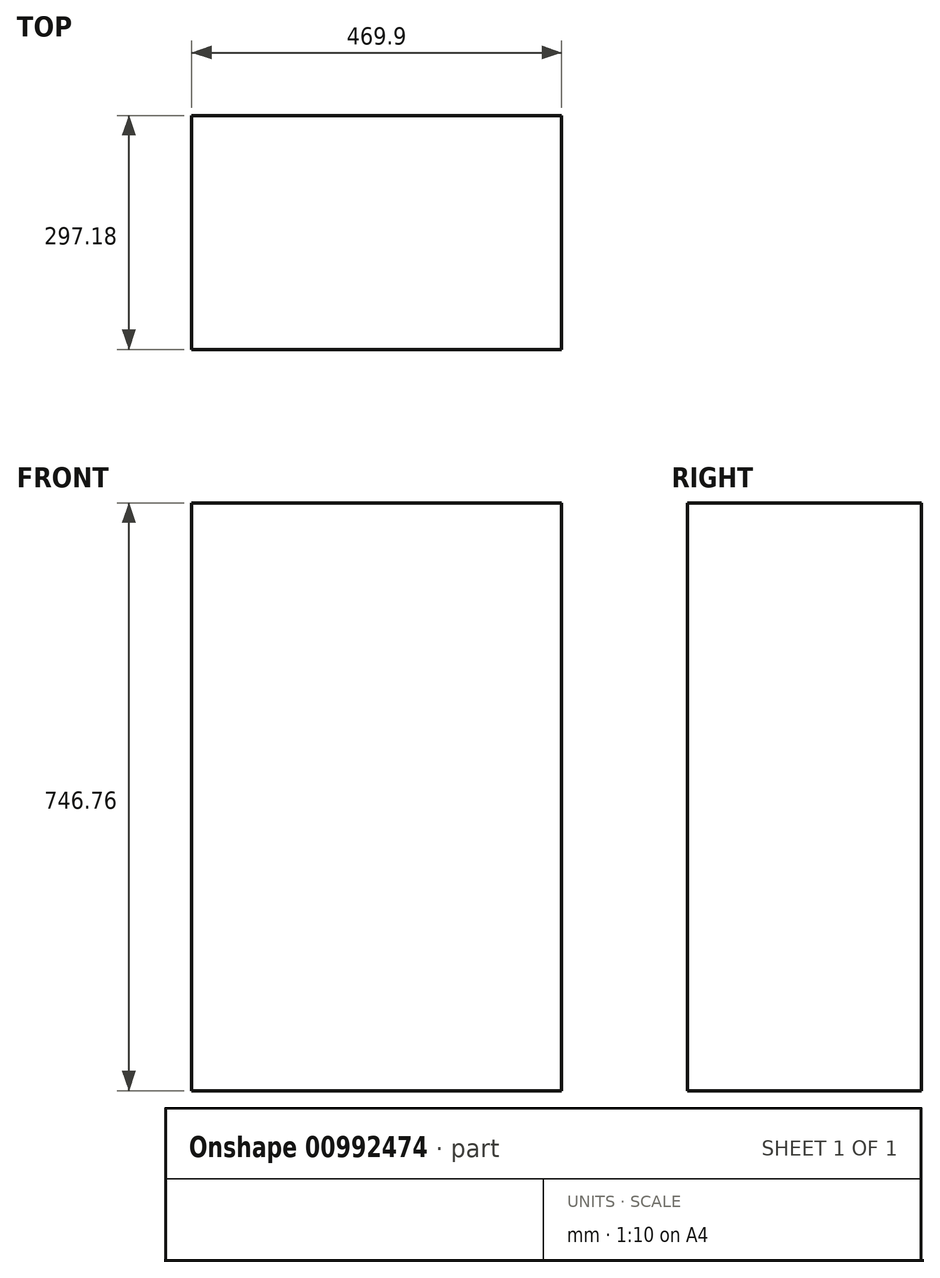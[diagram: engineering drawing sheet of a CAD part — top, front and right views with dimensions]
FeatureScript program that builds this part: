
annotation { "Feature Type Name" : "Feature", "Feature Type Description" : "" }
export const myFeature = defineFeature(function(context is Context, id is Id, definition is map)
    precondition{}
    {
        {
            var Q0;
            Q0=qCreatedBy(makeId("Front.planeOp"),FACE);
            var sketch = newSketch(context, id + "F0", { "sketchPlane" : qUnion([Q0])});
            skLineSegment(sketch, "E0.bottom", {"start": v(234.95, 373.38) * mm, "end": v(-234.95, 373.38) * mm});
            skLineSegment(sketch, "E0.top", {"start": v(234.95, -373.38) * mm, "end": v(-234.95, -373.38) * mm});
            skLineSegment(sketch, "E0.left", {"start": v(234.95, 373.38) * mm, "end": v(234.95, -373.38) * mm});
            skLineSegment(sketch, "E0.right", {"start": v(-234.95, 373.38) * mm, "end": v(-234.95, -373.38) * mm});
            skPoint(sketch, "E0.middle", {"position": v(0, 0) * mm});
            skSolve(sketch);
        }
        {
            var Q0;
            Q0 = qSketchRegion(id + "F0", true);
            extrude(context, id + "F1", {"entities" : qUnion([Q0]), "depth" : 297.18 * mm, "offsetDistance" : 25.4 * mm});
        }
    });
